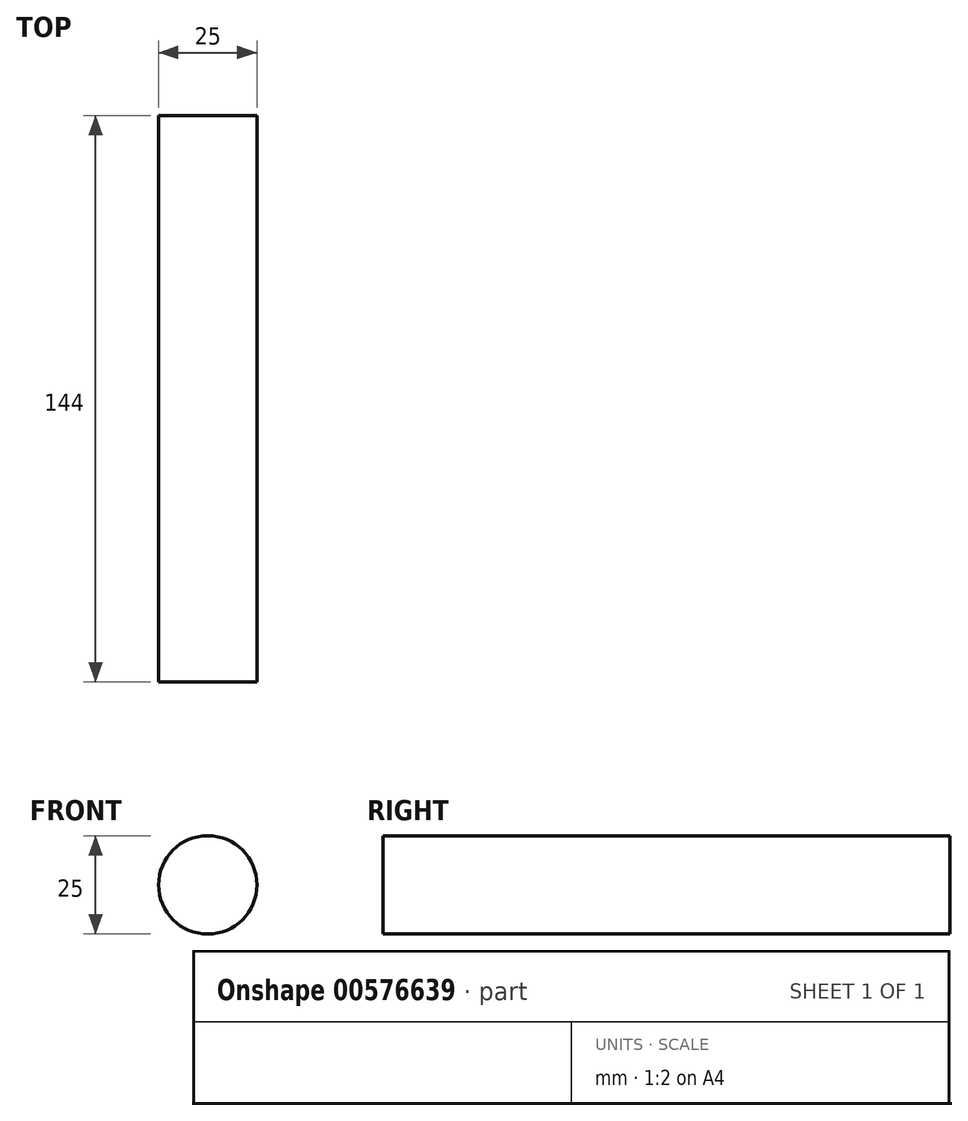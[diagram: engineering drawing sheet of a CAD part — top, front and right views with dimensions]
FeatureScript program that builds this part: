
annotation { "Feature Type Name" : "Feature", "Feature Type Description" : "" }
export const myFeature = defineFeature(function(context is Context, id is Id, definition is map)
    precondition{}
    {
        {
            var Q0;
            Q0=qCreatedBy(makeId("Front.planeOp"),FACE);
            var sketch = newSketch(context, id + "F0", { "sketchPlane" : qUnion([Q0])});
            skCircle(sketch, "E0", {"center": v(0, 0) * mm, "radius": 12.5 * mm});
            skSolve(sketch);
        }
        {
            var Q0;
            Q0 = qSketchRegion(id + "F0", true);
            extrude(context, id + "F1", {"entities" : qUnion([Q0]), "depth" : 144 * mm, "offsetDistance" : 25 * mm});
        }
    });
